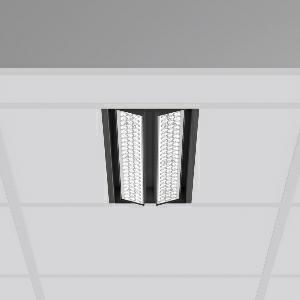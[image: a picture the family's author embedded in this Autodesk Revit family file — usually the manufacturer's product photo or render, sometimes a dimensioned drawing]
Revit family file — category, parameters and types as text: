
# Revit family: tx-move_901736_003_2_bb93
name_source: partatom
category: Lighting Fixtures
units: mm (PartAtom-declared; Revit-internal decimal feet)

## family parameters
Cut with Voids When Loaded = No
Host = Face
Light Source = No
Part Type = Normal
Room Calculation Point = No
Round Connector Dimension = Use Diameter
Shared = No

## types (1)
- MultiLumen 1 (1 x LED Modul 927, 2000 lm, 2700)
    Apparent Load = 32 VA
    Approval mark = CE
    CIE Flux Codes = 90 97 99 100 100
    Color Rendering = 92
    Color Temperature = 2700
    Default Elevation = 1800 mm
    Description = Series: TX-MOVE
Einlege/Einbau-Flächenstrahler. Housing: sheet steel, powder-coated. 2xSwivel range: 90°. High-efficiency LED units with optimum light control thanks to clear plastic (PC) lens optics. Spezielle Mikrostrukturen reduzieren Gelbsaum. Symmetrical light distribution. Best colour rendering with CRI >90 for fresh products and coloured textiles. Suitable for laying in grid ceiling module 625. Connected converter included in separate gearbox.Suitable for through-wiring.MultiLumen: Luminous flux adjustable in 3 steps. Accessories: Mounting frame for installation in suspended ceilings. Environmentally friendly and resource-saving due to replaceable and recyclable components. 
Colour: deep black, matt (RAL 9005)
Length: 622 mm
Width: 190 mm
Height: 39 mm
Cut-out length: 602 mm
Cut-out width: 174 mm
Recess height: 100 mm
Lamp: LED
Socket: without socket
Colour temperature: 2700K
Colour rendering index (CRI): 90
System power: 32 W
Rated luminous flux: 4000 lm
Luminous efficiency: 125 lm/W
System power 2: 43 W
Rated luminous flux 2: 5150 lm
Luminous efficiency 2: 120 lm/W
System power 3: 62 W
Rated luminous flux 3: 6750 lm
Luminous efficiency 3: 109 lm/W
Control gear: Regulated power supply
Protection class: I
Type of protection: IP 20
    Height = 0 mm  [stored 0 ft]
    Lamp = 1 x LED Modul 927
    Lamp Light Flux = 2000 lm
    Lamp count = 1
    Length = 622 mm
    Lifetime = 50000 h
    Luminous efficacy = 125 lm/W
    Manufacturer = RZB
    ModVariant = No
    Model = 901736.003.2
    Mounting Place = Ceiling, Wall
    Mounting Type = Recessed
    Number of Poles = 1
    OnlyDefault = Yes
    Power Factor = 1
    Product Name = TX-MOVE
    Product group = Recessed projectors
    ProductGroupID = 401
    Protection Class = Protection class I
    Protection Degree = IP 20
    RLX_Detail_Level = 1
    RLX_Emergency_Light_Flux = 0 lm
    RLX_Emergency_Type = 0
    RLX_Emergency_Type_DB = No
    RlxData = <blob elided: 35877 chars, md5=daf1959e>
    Socket = socket
    Standby Power = 0 W
    System Light Flux = 4000 lm
    System Power = 32 W
    Type Comments = MultiLumen 1
    Type Image = 901737.003.jpg
    URL = http://relux.com
    VarID = multilumen_1
    Voltage = 230 V
    Voltage Range = 220-240 V
    Weight = 0.00 kg
    Width = 190 mm  [stored 0.62336 ft]

note: [stored X ft] marks values corroborated as IEEE doubles in the binary element streams (Revit-internal decimal feet)

## geometry (parser evidence)
native form markers: Blend x4, Sweep x16
no freeform markers — native parametric forms only
